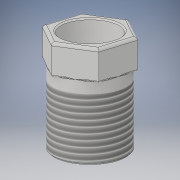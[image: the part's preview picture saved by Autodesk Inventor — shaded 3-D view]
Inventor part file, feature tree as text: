
AUTODESK INVENTOR PART (.ipt)
format: ipt  version: 2018 (Build 220112000, 112)  size: 307,712 bytes
history: native  units: mm
features: extrude x3, fillet x3, sketch x3, chamfer x1, thread x1
ambient origin geometry x8: Origin, YZ Plane, XZ Plane, XY Plane, X Axis, Y Axis, Z Axis, Center Point
bodies: Solid1 (feature_tree)
feature tree (11):
  extrude  "Extrusion1"  Depth=5.0mm TaperAngle=0.0deg
  extrude  "Extrusion2"  Depth=17.5mm TaperAngle=0.0deg
  extrude  "Extrusion3"  Depth=34.5mm TaperAngle=0.0deg
  chamfer  "Chamfer1"  Distance=0.25mm Angle=45.0deg
  thread  "Thread1"  [1 undecoded]
  fillet  "Fillet1"  Radius=0.5mm
  fillet  "Fillet2"  Radius=0.2mm
  fillet  "Fillet3"  Radius=0.2mm
  sketch  "Sketch1"  dims[d0=12.0mm d1=5.0mm d2=0.0mm]
  sketch  "Sketch2"  dims[d3=12.0mm d4=17.5mm d5=0.0mm]
  sketch  "Sketch3"  dims[d6=9.5mm d7=34.5mm d8=0.0mm d9=0.25mm d10=2.0mm d11=45.0deg d12=10.2mm d13=0.0mm d14=0.5mm d15=0.2mm d16=0.2mm]
note: 1 required parameter value undecoded (feature->parameter linkage not recoverable at this tier; creation-order binding heuristic only, values carry confidence <= 0.55)
